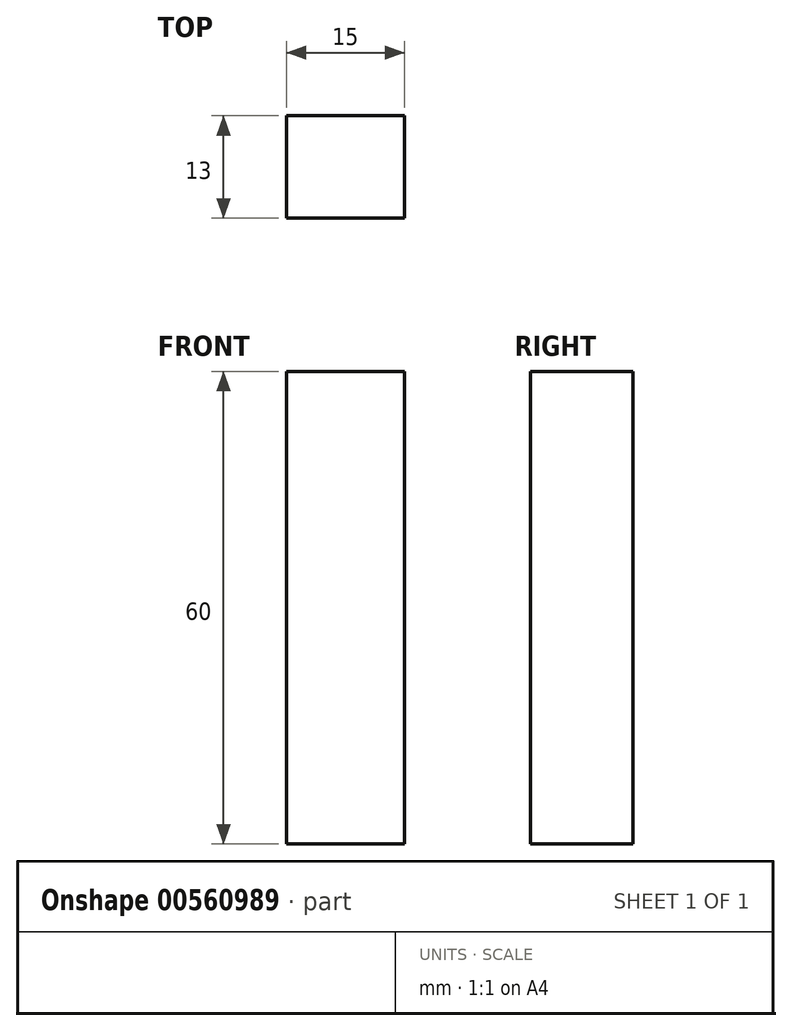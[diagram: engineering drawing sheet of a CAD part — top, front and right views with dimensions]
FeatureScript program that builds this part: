
annotation { "Feature Type Name" : "Feature", "Feature Type Description" : "" }
export const myFeature = defineFeature(function(context is Context, id is Id, definition is map)
    precondition{}
    {
        {
            var Q0;
            Q0=qCreatedBy(makeId("Front.planeOp"),FACE);
            var sketch = newSketch(context, id + "F0", { "sketchPlane" : qUnion([Q0])});
            skLineSegment(sketch, "E0.bottom", {"start": v(7.5, -30) * mm, "end": v(-7.5, -30) * mm});
            skLineSegment(sketch, "E0.top", {"start": v(7.5, 30) * mm, "end": v(-7.5, 30) * mm});
            skLineSegment(sketch, "E0.left", {"start": v(7.5, -30) * mm, "end": v(7.5, 30) * mm});
            skLineSegment(sketch, "E0.right", {"start": v(-7.5, -30) * mm, "end": v(-7.5, 30) * mm});
            skPoint(sketch, "E0.middle", {"position": v(0, 0) * mm});
            skSolve(sketch);
        }
        {
            var Q0;
            Q0=qSketchRegion(id+"F0",true);
            extrude(context, id + "F1", {"entities" : qUnion([Q0]), "endBound" : BoundingType.SYMMETRIC, "depth" : 13 * mm});
        }
    });
